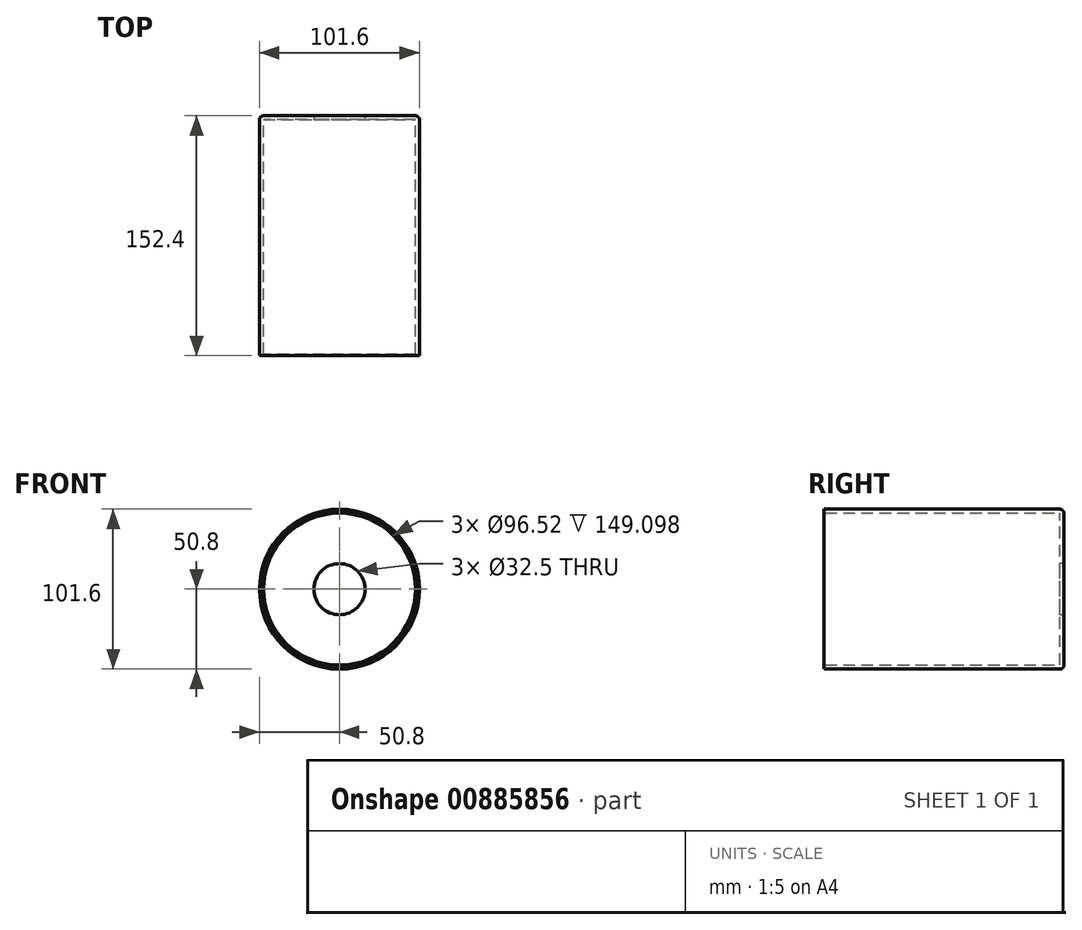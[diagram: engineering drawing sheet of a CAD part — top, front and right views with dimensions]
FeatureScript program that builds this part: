
annotation { "Feature Type Name" : "Feature", "Feature Type Description" : "" }
export const myFeature = defineFeature(function(context is Context, id is Id, definition is map)
    precondition{}
    {
        {
            var Q0;
            Q0=qCreatedBy(makeId("Front.planeOp"),FACE);
            var sketch = newSketch(context, id + "F0", { "sketchPlane" : qUnion([Q0])});
            skCircle(sketch, "E0", {"center": v(0, 0) * mm, "radius": 50.8 * mm});
            skSolve(sketch);
        }
        {
            var Q0;
            Q0=makeQuery(id+"F0.imprint","IMPRINT",FACE,{"disambiguationData":[TD([[makeQuery(id+"F0.imprint","IMPRINT",EDGE,{"derivedFrom":sQuery(id+"F0.wireOp",EDGE,"E0")}),1.0]])]});
            extrude(context, id + "F1", {"entities" : qUnion([Q0]), "depth" : 152.4 * mm, "offsetDistance" : 25.4 * mm});
        }
        {
            var Q0;
            Q0=makeQuery(id+"F1.opExtrude","CAP_FACE",FACE,{"disambiguationData":[OSD([sQuery(id+"F0.wireOp",EDGE,"E0")])],"isStart":false});
            shell(context, id + "F2", {"entities" : qUnion([Q0]), "thickness" : 2.54 * mm});
        }
        {
            var Q0;
            {var subQ0=sQuery(id+"F0.wireOp",EDGE,"E0");Q0=makeQuery(id+"F2.opShell","OFFSET_FACE",FACE,{"disambiguationData":[OSD([subQ0]),TDD([makeQuery(id+"F1.opExtrude","CAP_FACE",FACE,{"disambiguationData":[OSD([subQ0])],"isStart":true})])]});}
            var sketch = newSketch(context, id + "F3", { "sketchPlane" : qUnion([Q0])});
            skCircle(sketch, "E1", {"center": v(0, 0) * mm, "radius": 16.25 * mm});
            skSolve(sketch);
        }
        {
            var Q0;
            Q0=makeQuery(id+"F3.imprint","IMPRINT",FACE,{"disambiguationData":[TD([[makeQuery(id+"F3.imprint","IMPRINT",EDGE,{"derivedFrom":sQuery(id+"F3.wireOp",EDGE,"E1")}),1.0]])]});
            extrude(context, id + "F4", {"entities" : qUnion([Q0]), "operationType" : NewBodyOperationType.REMOVE, "oppositeDirection" : true, "depth" : 25.4 * mm, "offsetDistance" : 25.4 * mm, "hasSecondDirection" : true, "secondDirectionOppositeDirection" : false, "secondDirectionDepth" : 25.4 * mm});
        }
        {
            var Q0;
            {var subQ0=sQuery(id+"F0.wireOp",EDGE,"E0");Q0=makeQuery(id+"F2.opShell","OFFSET_EDGE",EDGE,{"disambiguationData":[OSD([subQ0]),TDD([makeQuery(id+"F1.opExtrude","CAP_EDGE",EDGE,{"disambiguationData":[OSD([subQ0])],"isStart":false})])]});}
            chamfer(context, id + "F5", {"entities" : qUnion([Q0]), "width" : 0.76 * mm, "tangentPropagation" : true});
        }
        {
            var Q0;
            Q0=makeQuery(id+"F1.opExtrude","CAP_EDGE",EDGE,{"disambiguationData":[OSD([sQuery(id+"F0.wireOp",EDGE,"E0")])],"isStart":true});
            fillet(context, id + "F6", {"entities" : qUnion([Q0]), "radius" : 2.54 * mm, "tangentPropagation" : true, "allowEdgeOverflow" : false});
        }
    });
